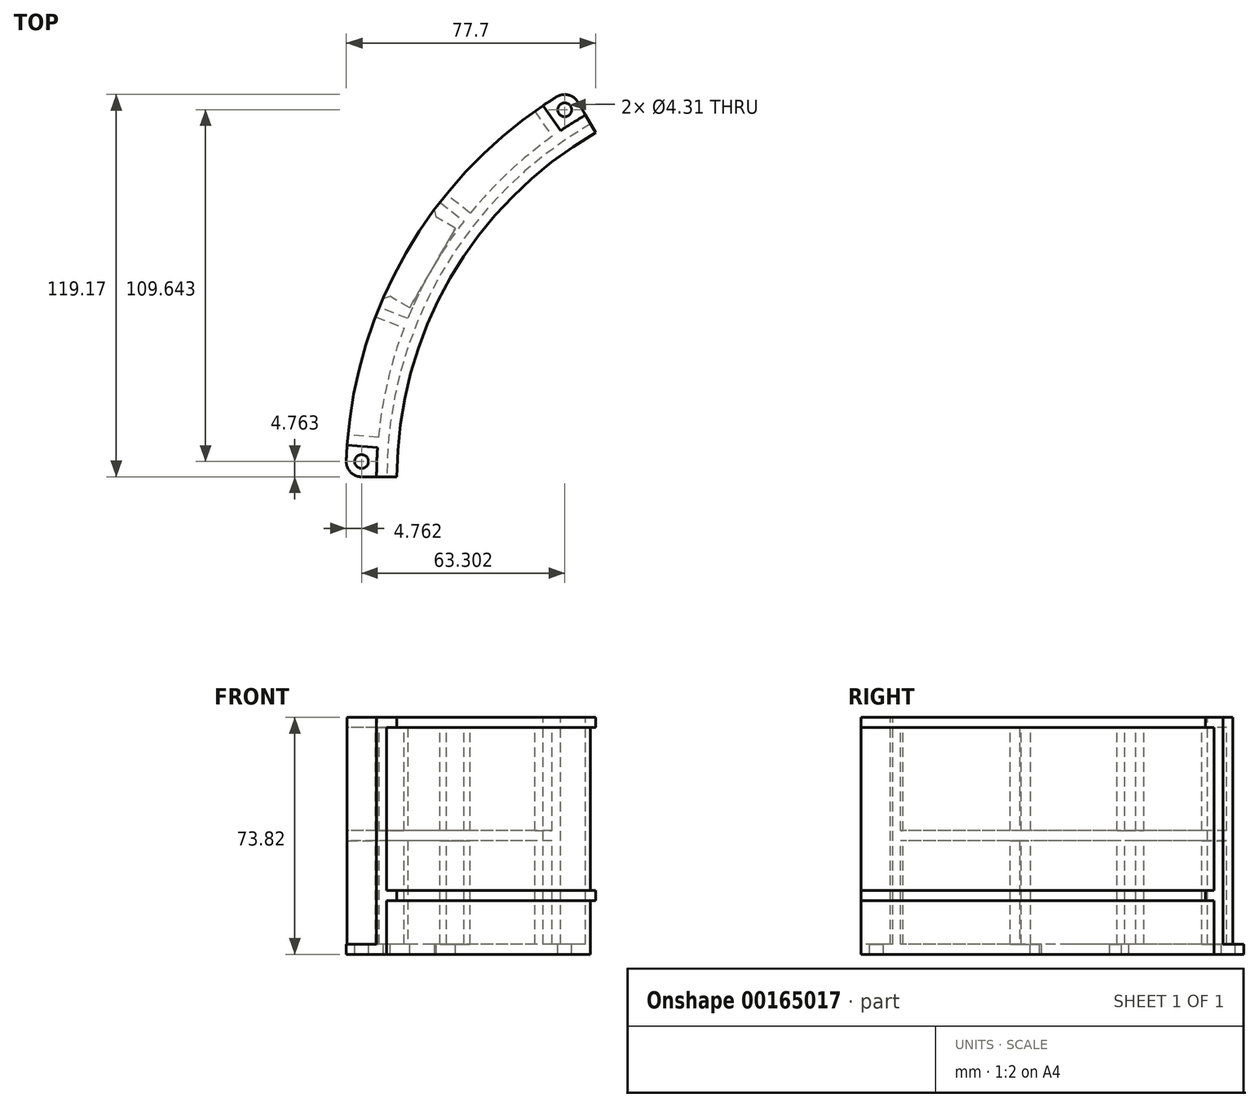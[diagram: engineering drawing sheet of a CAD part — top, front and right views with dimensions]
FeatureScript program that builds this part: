
annotation { "Feature Type Name" : "Feature", "Feature Type Description" : "" }
export const myFeature = defineFeature(function(context is Context, id is Id, definition is map)
    precondition{}
    {
        {
            var Q0;
            Q0=qCreatedBy(makeId("Top.planeOp"),FACE);
            var sketch = newSketch(context, id + "F0", { "sketchPlane" : qUnion([Q0])});
            skLineSegment(sketch, "E0", {"start": v(0, 0) * mm, "end": v(123.83, 0) * mm, "construction": true});
            skLineSegment(sketch, "E1", {"start": v(123.83, 0) * mm, "end": v(61.91, 107.24) * mm, "construction": true});
            skArc(sketch, "E2", {"start": v(61.91, 107.24) * mm, "mid": v(16.59, 61.91) * mm, "end": v(0, 0) * mm});
            skLineSegment(sketch, "E3", {"start": v(0, 0) * mm, "end": v(-15.87, 0) * mm});
            skLineSegment(sketch, "E4", {"start": v(61.91, 107.24) * mm, "end": v(53.97, 120.98) * mm});
            skArc(sketch, "E5", {"start": v(53.97, 120.98) * mm, "mid": v(2.84, 69.85) * mm, "end": v(-15.88, 0) * mm});
            skSolve(sketch);
        }
        {
            var Q0;
            Q0 = qSketchRegion(id + "F0", true);
            extrude(context, id + "F1", {"entities" : qUnion([Q0]), "depth" : 73.82 * mm});
        }
        {
            var Q0;
            Q0=makeQuery(id+"F1.opExtrude","SWEPT_FACE",FACE,{"disambiguationData":[OSD([sQuery(id+"F0.wireOp",EDGE,"E3")])]});
            var sketch = newSketch(context, id + "F2", { "sketchPlane" : qUnion([Q0])});
            skLineSegment(sketch, "E6.bottom", {"start": v(0, 70.64) * mm, "end": v(-3.18, 70.64) * mm});
            skLineSegment(sketch, "E6.top", {"start": v(0, 19.84) * mm, "end": v(-3.18, 19.84) * mm});
            skLineSegment(sketch, "E6.left", {"start": v(0, 70.64) * mm, "end": v(0, 19.84) * mm});
            skLineSegment(sketch, "E6.right", {"start": v(-3.18, 70.64) * mm, "end": v(-3.17, 19.84) * mm});
            skLineSegment(sketch, "E7.bottom", {"start": v(0, 0) * mm, "end": v(-3.18, 0) * mm});
            skLineSegment(sketch, "E7.top", {"start": v(0, 16.67) * mm, "end": v(-3.18, 16.67) * mm});
            skLineSegment(sketch, "E7.left", {"start": v(0, 0) * mm, "end": v(0, 16.67) * mm});
            skLineSegment(sketch, "E7.right", {"start": v(-3.18, 0) * mm, "end": v(-3.18, 16.67) * mm});
            skLineSegment(sketch, "E8", {"start": v(-1.59, 70.64) * mm, "end": v(-1.59, 73.82) * mm, "construction": true});
            skLineSegment(sketch, "E9", {"start": v(-1.59, 19.84) * mm, "end": v(-1.59, 16.67) * mm, "construction": true});
            skLineSegment(sketch, "E10", {"start": v(-3.18, 8.33) * mm, "end": v(-6.35, 8.33) * mm, "construction": true});
            skLineSegment(sketch, "E11", {"start": v(-11.11, 3.17) * mm, "end": v(-11.11, 0) * mm, "construction": true});
            skLineSegment(sketch, "E12.bottom", {"start": v(-6.35, 3.17) * mm, "end": v(-15.87, 3.17) * mm});
            skLineSegment(sketch, "E12.top", {"start": v(-6.35, 35.32) * mm, "end": v(-15.88, 35.32) * mm});
            skLineSegment(sketch, "E12.left", {"start": v(-6.35, 3.17) * mm, "end": v(-6.35, 35.32) * mm});
            skLineSegment(sketch, "E12.right", {"start": v(-15.87, 3.17) * mm, "end": v(-15.87, 35.32) * mm});
            skLineSegment(sketch, "E13.bottom", {"start": v(-15.88, 70.64) * mm, "end": v(-6.35, 70.64) * mm});
            skLineSegment(sketch, "E13.top", {"start": v(-15.88, 38.5) * mm, "end": v(-6.35, 38.5) * mm});
            skLineSegment(sketch, "E13.left", {"start": v(-15.87, 70.64) * mm, "end": v(-15.87, 38.5) * mm});
            skLineSegment(sketch, "E13.right", {"start": v(-6.35, 70.64) * mm, "end": v(-6.35, 38.5) * mm});
            skLineSegment(sketch, "E14", {"start": v(-11.11, 70.64) * mm, "end": v(-11.11, 73.82) * mm, "construction": true});
            skLineSegment(sketch, "E15", {"start": v(-11.11, 38.5) * mm, "end": v(-11.11, 35.32) * mm, "construction": true});
            skLineSegment(sketch, "E16", {"start": v(-6.35, 54.57) * mm, "end": v(-3.18, 54.57) * mm, "construction": true});
            skSolve(sketch);
        }
        {
            var Q0;
            Q0 = qSketchRegion(id + "F2", true);
            var Q1;
            Q1=makeQuery(id+"F1.opExtrude","SWEPT_FACE",FACE,{"disambiguationData":[OSD([sQuery(id+"F0.wireOp",EDGE,"E2")])]});
            revolve(context, id + "F3", {"operationType" : NewBodyOperationType.REMOVE, "entities" : qUnion([Q0]), "axis" : qUnion([Q1]), "revolveType" : RevolveType.FULL, "oppositeDirection" : true});
        }
        {
            var Q0;
            Q0=makeQuery(id+"F1.opExtrude","CAP_FACE",FACE,{"disambiguationData":[OSD([sQuery(id+"F0.wireOp",EDGE,"E2"),sQuery(id+"F0.wireOp",EDGE,"E3"),sQuery(id+"F0.wireOp",EDGE,"E4"),sQuery(id+"F0.wireOp",EDGE,"E5")])],"isStart":false});
            var sketch = newSketch(context, id + "F4", { "sketchPlane" : qUnion([Q0])});
            skLineSegment(sketch, "E17.bottom", {"start": v(-15.26, 13.08) * mm, "end": v(-5.77, 12.3) * mm});
            skLineSegment(sketch, "E17.top", {"start": v(-15.52, 9.91) * mm, "end": v(-6.03, 9.13) * mm});
            skLineSegment(sketch, "E17.left", {"start": v(-15.26, 13.08) * mm, "end": v(-15.52, 9.91) * mm, "construction": true});
            skLineSegment(sketch, "E17.right", {"start": v(-5.77, 12.3) * mm, "end": v(-6.03, 9.13) * mm, "construction": true});
            skLineSegment(sketch, "E18", {"start": v(-5.9, 10.71) * mm, "end": v(123.83, 0) * mm, "construction": true});
            skArc(sketch, "E19", {"start": v(-5.77, 12.3) * mm, "mid": v(-5.9, 10.71) * mm, "end": v(-6.03, 9.13) * mm});
            skArc(sketch, "E20", {"start": v(-15.26, 13.08) * mm, "mid": v(-15.4, 11.5) * mm, "end": v(-15.52, 9.91) * mm});
            skCircle(sketch, "E21", {"center": v(-11.03, 4.76) * mm, "radius": 4.76 * mm, "construction": true});
            skLineSegment(sketch, "E22", {"start": v(123.83, 0) * mm, "end": v(16.59, 61.91) * mm, "construction": true});
            skLineSegment(sketch, "E23.bottom", {"start": v(15.38, 88.06) * mm, "end": v(22.84, 82.14) * mm});
            skLineSegment(sketch, "E23.top", {"start": v(13.4, 85.58) * mm, "end": v(20.87, 79.66) * mm});
            skLineSegment(sketch, "E23.left", {"start": v(13.4, 85.58) * mm, "end": v(15.38, 88.06) * mm, "construction": true});
            skLineSegment(sketch, "E23.right", {"start": v(20.87, 79.66) * mm, "end": v(22.84, 82.14) * mm, "construction": true});
            skArc(sketch, "E24", {"start": v(15.38, 88.06) * mm, "mid": v(14.38, 86.83) * mm, "end": v(13.4, 85.58) * mm});
            skArc(sketch, "E25", {"start": v(22.84, 82.14) * mm, "mid": v(21.84, 80.9) * mm, "end": v(20.87, 79.66) * mm});
            skLineSegment(sketch, "E26", {"start": v(49.69, 106.99) * mm, "end": v(123.82, 0) * mm, "construction": true});
            skLineSegment(sketch, "E27.bottom", {"start": v(51, 107.9) * mm, "end": v(45.57, 115.72) * mm});
            skLineSegment(sketch, "E27.top", {"start": v(48.38, 106.09) * mm, "end": v(42.96, 113.91) * mm});
            skLineSegment(sketch, "E27.left", {"start": v(45.57, 115.72) * mm, "end": v(42.96, 113.91) * mm, "construction": true});
            skLineSegment(sketch, "E27.right", {"start": v(51, 107.9) * mm, "end": v(48.38, 106.09) * mm, "construction": true});
            skArc(sketch, "E28", {"start": v(51, 107.9) * mm, "mid": v(49.68, 107) * mm, "end": v(48.38, 106.09) * mm});
            skArc(sketch, "E29", {"start": v(45.57, 115.72) * mm, "mid": v(44.26, 114.83) * mm, "end": v(42.96, 113.91) * mm});
            skLineSegment(sketch, "E30", {"start": v(123.83, 0) * mm, "end": v(2.78, 47.86) * mm, "construction": true});
            skLineSegment(sketch, "E31.bottom", {"start": v(2.2, 46.38) * mm, "end": v(3.36, 49.34) * mm, "construction": true});
            skLineSegment(sketch, "E31.top", {"start": v(-6.66, 49.89) * mm, "end": v(-5.5, 52.84) * mm, "construction": true});
            skLineSegment(sketch, "E31.left", {"start": v(2.2, 46.38) * mm, "end": v(-6.66, 49.89) * mm});
            skLineSegment(sketch, "E31.right", {"start": v(3.36, 49.34) * mm, "end": v(-5.5, 52.84) * mm});
            skArc(sketch, "E32", {"start": v(-5.5, 52.84) * mm, "mid": v(-6.09, 51.37) * mm, "end": v(-6.66, 49.89) * mm});
            skArc(sketch, "E33", {"start": v(3.36, 49.34) * mm, "mid": v(2.77, 47.86) * mm, "end": v(2.2, 46.38) * mm});
            skLineSegment(sketch, "E34", {"start": v(21.85, 80.9) * mm, "end": v(123.83, 0) * mm, "construction": true});
            skLineSegment(sketch, "E35", {"start": v(2.78, 47.86) * mm, "end": v(16.59, 61.91) * mm, "construction": true});
            skLineSegment(sketch, "E36", {"start": v(21.85, 80.9) * mm, "end": v(16.59, 61.91) * mm, "construction": true});
            skLineSegment(sketch, "E37", {"start": v(58.96, 5.36) * mm, "end": v(63.3, 23.93) * mm, "construction": true});
            skLineSegment(sketch, "E38", {"start": v(63.3, 23.93) * mm, "end": v(72.84, 40.45) * mm, "construction": true});
            skLineSegment(sketch, "E39", {"start": v(72.84, 40.45) * mm, "end": v(86.76, 53.5) * mm, "construction": true});
            skSolve(sketch);
        }
        {
            var Q0;
            Q0 = qSketchRegion(id + "F4", true);
            var Q1;
            Q1=makeQuery(id+"F1.opExtrude","CAP_FACE",FACE,{"disambiguationData":[OSD([sQuery(id+"F0.wireOp",EDGE,"E2"),sQuery(id+"F0.wireOp",EDGE,"E3"),sQuery(id+"F0.wireOp",EDGE,"E4"),sQuery(id+"F0.wireOp",EDGE,"E5")])],"isStart":true});
            extrude(context, id + "F5", {"entities" : qUnion([Q0]), "operationType" : NewBodyOperationType.ADD, "endBound" : BoundingType.UP_TO_SURFACE, "oppositeDirection" : true, "endBoundEntityFace" : qUnion([Q1]), "depth" : 25.4 * mm});
        }
        {
            var Q0;
            Q0=makeQuery(id+"F5.boolean.opBoolean","SPLIT",FACE,{"disambiguationData":[TD([makeQuery(id+"F1.opExtrude","SWEPT_FACE",FACE,{"disambiguationData":[OSD([sQuery(id+"F0.wireOp",EDGE,"E3")])]})])],"derivedFrom":makeQuery(id+"F3.boolean.opBoolean","COPY",FACE,{"derivedFrom":makeQuery(id+"F3.opRevolve","SWEPT_FACE",FACE,{"disambiguationData":[OSD([sQuery(id+"F2.wireOp",EDGE,"E12.bottom")])]})})});
            var sketch = newSketch(context, id + "F6", { "sketchPlane" : qUnion([Q0])});
            skCircle(sketch, "E40", {"center": v(52.27, 114.4) * mm, "radius": 4.76 * mm, "construction": true});
            skCircle(sketch, "E41", {"center": v(52.27, 114.4) * mm, "radius": 2.15 * mm});
            skCircle(sketch, "E42", {"center": v(-11.03, 4.76) * mm, "radius": 4.76 * mm, "construction": true});
            skCircle(sketch, "E43", {"center": v(-11.03, 4.76) * mm, "radius": 2.15 * mm});
            skSolve(sketch);
        }
        {
            var Q0;
            Q0 = qSketchRegion(id + "F6", true);
            var Q1;
            Q1=makeQuery(id+"F1.opExtrude","CAP_FACE",FACE,{"disambiguationData":[OSD([sQuery(id+"F0.wireOp",EDGE,"E2"),sQuery(id+"F0.wireOp",EDGE,"E3"),sQuery(id+"F0.wireOp",EDGE,"E4"),sQuery(id+"F0.wireOp",EDGE,"E5")])],"isStart":true});
            extrude(context, id + "F7", {"entities" : qUnion([Q0]), "operationType" : NewBodyOperationType.REMOVE, "endBound" : BoundingType.UP_TO_SURFACE, "oppositeDirection" : true, "endBoundEntityFace" : qUnion([Q1]), "depth" : 25.4 * mm});
        }
        {
            var Q0;
            {var subQ0=sQuery(id+"F0.wireOp",EDGE,"E5");var subQ1=sQuery(id+"F0.wireOp",EDGE,"E4");Q0=makeQuery(id+"F3.boolean.opBoolean","SPLIT",EDGE,{"disambiguationData":[TD([makeQuery(id+"F3.opRevolve","SWEPT_FACE",FACE,{"disambiguationData":[OSD([sQuery(id+"F2.wireOp",EDGE,"E12.bottom")])]})])],"derivedFrom":makeQuery(id+"F1.opExtrude","SWEPT_EDGE",EDGE,{"disambiguationData":[OSD([subQ1,subQ0])]})});}
            var Q1;
            {var subQ0=sQuery(id+"F0.wireOp",EDGE,"E5");var subQ1=sQuery(id+"F0.wireOp",EDGE,"E3");Q1=makeQuery(id+"F3.boolean.opBoolean","SPLIT",EDGE,{"disambiguationData":[TD([makeQuery(id+"F3.opRevolve","SWEPT_FACE",FACE,{"disambiguationData":[OSD([sQuery(id+"F2.wireOp",EDGE,"E12.bottom")])]})])],"derivedFrom":makeQuery(id+"F1.opExtrude","SWEPT_EDGE",EDGE,{"disambiguationData":[OSD([subQ1,subQ0])]})});}
            var Q2;
            {var subQ0=sQuery(id+"F0.wireOp",EDGE,"E3");var subQ1=sQuery(id+"F0.wireOp",EDGE,"E5");Q2=makeQuery(id+"F3.boolean.opBoolean","SPLIT",EDGE,{"disambiguationData":[TD([makeQuery(id+"F3.opRevolve","SWEPT_FACE",FACE,{"disambiguationData":[OSD([sQuery(id+"F2.wireOp",EDGE,"E12.top")])]})])],"derivedFrom":makeQuery(id+"F1.opExtrude","SWEPT_EDGE",EDGE,{"disambiguationData":[OSD([subQ0,subQ1])]})});}
            var Q3;
            {var subQ0=sQuery(id+"F0.wireOp",EDGE,"E5");var subQ1=sQuery(id+"F0.wireOp",EDGE,"E3");Q3=makeQuery(id+"F3.boolean.opBoolean","SPLIT",EDGE,{"disambiguationData":[TD([makeQuery(id+"F3.opRevolve","SWEPT_FACE",FACE,{"disambiguationData":[OSD([sQuery(id+"F2.wireOp",EDGE,"E13.bottom")])]})])],"derivedFrom":makeQuery(id+"F1.opExtrude","SWEPT_EDGE",EDGE,{"disambiguationData":[OSD([subQ1,subQ0])]})});}
            var Q4;
            {var subQ0=sQuery(id+"F0.wireOp",EDGE,"E4");var subQ1=sQuery(id+"F0.wireOp",EDGE,"E5");Q4=makeQuery(id+"F3.boolean.opBoolean","SPLIT",EDGE,{"disambiguationData":[TD([makeQuery(id+"F3.opRevolve","SWEPT_FACE",FACE,{"disambiguationData":[OSD([sQuery(id+"F2.wireOp",EDGE,"E12.top")])]})])],"derivedFrom":makeQuery(id+"F1.opExtrude","SWEPT_EDGE",EDGE,{"disambiguationData":[OSD([subQ0,subQ1])]})});}
            var Q5;
            {var subQ0=sQuery(id+"F0.wireOp",EDGE,"E5");var subQ1=sQuery(id+"F0.wireOp",EDGE,"E4");Q5=makeQuery(id+"F3.boolean.opBoolean","SPLIT",EDGE,{"disambiguationData":[TD([makeQuery(id+"F3.opRevolve","SWEPT_FACE",FACE,{"disambiguationData":[OSD([sQuery(id+"F2.wireOp",EDGE,"E13.bottom")])]})])],"derivedFrom":makeQuery(id+"F1.opExtrude","SWEPT_EDGE",EDGE,{"disambiguationData":[OSD([subQ1,subQ0])]})});}
            fillet(context, id + "F8", {"entities" : qUnion([Q0, Q1, Q2, Q3, Q4, Q5]), "radius" : 4.76 * mm, "tangentPropagation" : true, "allowEdgeOverflow" : false});
        }
        {
            var Q0;
            Q0=makeQuery(id+"F5.boolean.opBoolean","SPLIT",FACE,{"disambiguationData":[TD([makeQuery(id+"F5.opExtrude","SWEPT_FACE",FACE,{"disambiguationData":[OSD([sQuery(id+"F4.wireOp",EDGE,"E23.top")])]})])],"derivedFrom":makeQuery(id+"F3.boolean.opBoolean","COPY",FACE,{"derivedFrom":makeQuery(id+"F3.opRevolve","SWEPT_FACE",FACE,{"disambiguationData":[OSD([sQuery(id+"F2.wireOp",EDGE,"E12.bottom")])]})})});
            var sketch = newSketch(context, id + "F9", { "sketchPlane" : qUnion([Q0])});
            skLineSegment(sketch, "E44.bottom", {"start": v(3.95, 52.71) * mm, "end": v(-4.3, 57.48) * mm});
            skLineSegment(sketch, "E44.top", {"start": v(18.23, 77.46) * mm, "end": v(9.99, 82.22) * mm});
            skLineSegment(sketch, "E44.left", {"start": v(18.23, 77.46) * mm, "end": v(3.95, 52.71) * mm});
            skLineSegment(sketch, "E44.right", {"start": v(9.99, 82.22) * mm, "end": v(-4.3, 57.48) * mm});
            skLineSegment(sketch, "E45", {"start": v(11.1, 65.09) * mm, "end": v(123.82, 0) * mm, "construction": true});
            skSolve(sketch);
        }
        {
            var Q0;
            Q0 = qSketchRegion(id + "F9", true);
            var Q1;
            Q1=makeQuery(id+"F1.opExtrude","CAP_FACE",FACE,{"disambiguationData":[OSD([sQuery(id+"F0.wireOp",EDGE,"E2"),sQuery(id+"F0.wireOp",EDGE,"E3"),sQuery(id+"F0.wireOp",EDGE,"E4"),sQuery(id+"F0.wireOp",EDGE,"E5")])],"isStart":true});
            extrude(context, id + "F10", {"entities" : qUnion([Q0]), "operationType" : NewBodyOperationType.REMOVE, "endBound" : BoundingType.UP_TO_SURFACE, "oppositeDirection" : true, "endBoundEntityFace" : qUnion([Q1]), "depth" : 25.4 * mm});
        }
        {
            var Q0;
            {var subQ4=sQuery(id+"F0.wireOp",EDGE,"E5");var subQ5=makeQuery(id+"F1.opExtrude","SWEPT_FACE",FACE,{"disambiguationData":[OSD([subQ4])]});Q0=makeQuery(id+"F10.boolean.opBoolean","INTERSECT",EDGE,{"derivedFrom":[makeQuery(id+"F5.boolean.opBoolean","MERGE",FACE,{"derivedFrom":[makeQuery(id+"F3.boolean.opBoolean","SPLIT",FACE,{"disambiguationData":[TD([makeQuery(id+"F3.opRevolve","SWEPT_FACE",FACE,{"disambiguationData":[OSD([sQuery(id+"F2.wireOp",EDGE,"E12.bottom")])]})])],"derivedFrom":subQ5}),makeQuery(id+"F3.boolean.opBoolean","SPLIT",FACE,{"disambiguationData":[TD([makeQuery(id+"F3.opRevolve","SWEPT_FACE",FACE,{"disambiguationData":[OSD([sQuery(id+"F2.wireOp",EDGE,"E13.bottom")])]})])],"derivedFrom":subQ5}),makeQuery(id+"F3.boolean.opBoolean","SPLIT",FACE,{"disambiguationData":[TD([makeQuery(id+"F3.opRevolve","SWEPT_FACE",FACE,{"disambiguationData":[OSD([sQuery(id+"F2.wireOp",EDGE,"E12.top")])]})])],"derivedFrom":subQ5}),makeQuery(id+"F5.opExtrude","SWEPT_FACE",FACE,{"disambiguationData":[OSD([sQuery(id+"F4.wireOp",EDGE,"E20")])]}),makeQuery(id+"F5.opExtrude","SWEPT_FACE",FACE,{"disambiguationData":[OSD([sQuery(id+"F4.wireOp",EDGE,"E24")])]}),makeQuery(id+"F5.opExtrude","SWEPT_FACE",FACE,{"disambiguationData":[OSD([sQuery(id+"F4.wireOp",EDGE,"E29")])]}),makeQuery(id+"F5.opExtrude","SWEPT_FACE",FACE,{"disambiguationData":[OSD([sQuery(id+"F4.wireOp",EDGE,"E32")])]})]}),makeQuery(id+"F10.opExtrude","SWEPT_FACE",FACE,{"disambiguationData":[OSD([sQuery(id+"F9.wireOp",EDGE,"E44.top")])]})]});}
            var Q1;
            {var subQ4=sQuery(id+"F0.wireOp",EDGE,"E5");var subQ5=makeQuery(id+"F1.opExtrude","SWEPT_FACE",FACE,{"disambiguationData":[OSD([subQ4])]});Q1=makeQuery(id+"F10.boolean.opBoolean","INTERSECT",EDGE,{"derivedFrom":[makeQuery(id+"F5.boolean.opBoolean","MERGE",FACE,{"derivedFrom":[makeQuery(id+"F3.boolean.opBoolean","SPLIT",FACE,{"disambiguationData":[TD([makeQuery(id+"F3.opRevolve","SWEPT_FACE",FACE,{"disambiguationData":[OSD([sQuery(id+"F2.wireOp",EDGE,"E12.bottom")])]})])],"derivedFrom":subQ5}),makeQuery(id+"F3.boolean.opBoolean","SPLIT",FACE,{"disambiguationData":[TD([makeQuery(id+"F3.opRevolve","SWEPT_FACE",FACE,{"disambiguationData":[OSD([sQuery(id+"F2.wireOp",EDGE,"E13.bottom")])]})])],"derivedFrom":subQ5}),makeQuery(id+"F3.boolean.opBoolean","SPLIT",FACE,{"disambiguationData":[TD([makeQuery(id+"F3.opRevolve","SWEPT_FACE",FACE,{"disambiguationData":[OSD([sQuery(id+"F2.wireOp",EDGE,"E12.top")])]})])],"derivedFrom":subQ5}),makeQuery(id+"F5.opExtrude","SWEPT_FACE",FACE,{"disambiguationData":[OSD([sQuery(id+"F4.wireOp",EDGE,"E20")])]}),makeQuery(id+"F5.opExtrude","SWEPT_FACE",FACE,{"disambiguationData":[OSD([sQuery(id+"F4.wireOp",EDGE,"E24")])]}),makeQuery(id+"F5.opExtrude","SWEPT_FACE",FACE,{"disambiguationData":[OSD([sQuery(id+"F4.wireOp",EDGE,"E29")])]}),makeQuery(id+"F5.opExtrude","SWEPT_FACE",FACE,{"disambiguationData":[OSD([sQuery(id+"F4.wireOp",EDGE,"E32")])]})]}),makeQuery(id+"F10.opExtrude","SWEPT_FACE",FACE,{"disambiguationData":[OSD([sQuery(id+"F9.wireOp",EDGE,"E44.bottom")])]})]});}
            chamfer(context, id + "F11", {"entities" : qUnion([Q0, Q1]), "width" : 1.59 * mm, "tangentPropagation" : true});
        }
        {
            var Q0;
            Q0=makeQuery(id+"F5.boolean.opBoolean","SPLIT",FACE,{"disambiguationData":[TD([makeQuery(id+"F1.opExtrude","SWEPT_FACE",FACE,{"disambiguationData":[OSD([sQuery(id+"F0.wireOp",EDGE,"E4")])]})])],"derivedFrom":makeQuery(id+"F3.boolean.opBoolean","COPY",FACE,{"derivedFrom":makeQuery(id+"F3.opRevolve","SWEPT_FACE",FACE,{"disambiguationData":[OSD([sQuery(id+"F2.wireOp",EDGE,"E12.top")])]})})});
            var Q1;
            Q1=makeQuery(id+"F5.boolean.opBoolean","SPLIT",FACE,{"disambiguationData":[TD([makeQuery(id+"F1.opExtrude","SWEPT_FACE",FACE,{"disambiguationData":[OSD([sQuery(id+"F0.wireOp",EDGE,"E3")])]})])],"derivedFrom":makeQuery(id+"F3.boolean.opBoolean","COPY",FACE,{"derivedFrom":makeQuery(id+"F3.opRevolve","SWEPT_FACE",FACE,{"disambiguationData":[OSD([sQuery(id+"F2.wireOp",EDGE,"E12.top")])]})})});
            var Q2;
            Q2=makeQuery(id+"F1.opExtrude","CAP_FACE",FACE,{"disambiguationData":[OSD([sQuery(id+"F0.wireOp",EDGE,"E2"),sQuery(id+"F0.wireOp",EDGE,"E3"),sQuery(id+"F0.wireOp",EDGE,"E4"),sQuery(id+"F0.wireOp",EDGE,"E5")])],"isStart":false});
            extrude(context, id + "F12", {"entities" : qUnion([Q0, Q1]), "operationType" : NewBodyOperationType.REMOVE, "endBound" : BoundingType.UP_TO_SURFACE, "oppositeDirection" : true, "endBoundEntityFace" : qUnion([Q2]), "depth" : 25.4 * mm});
        }
    });
